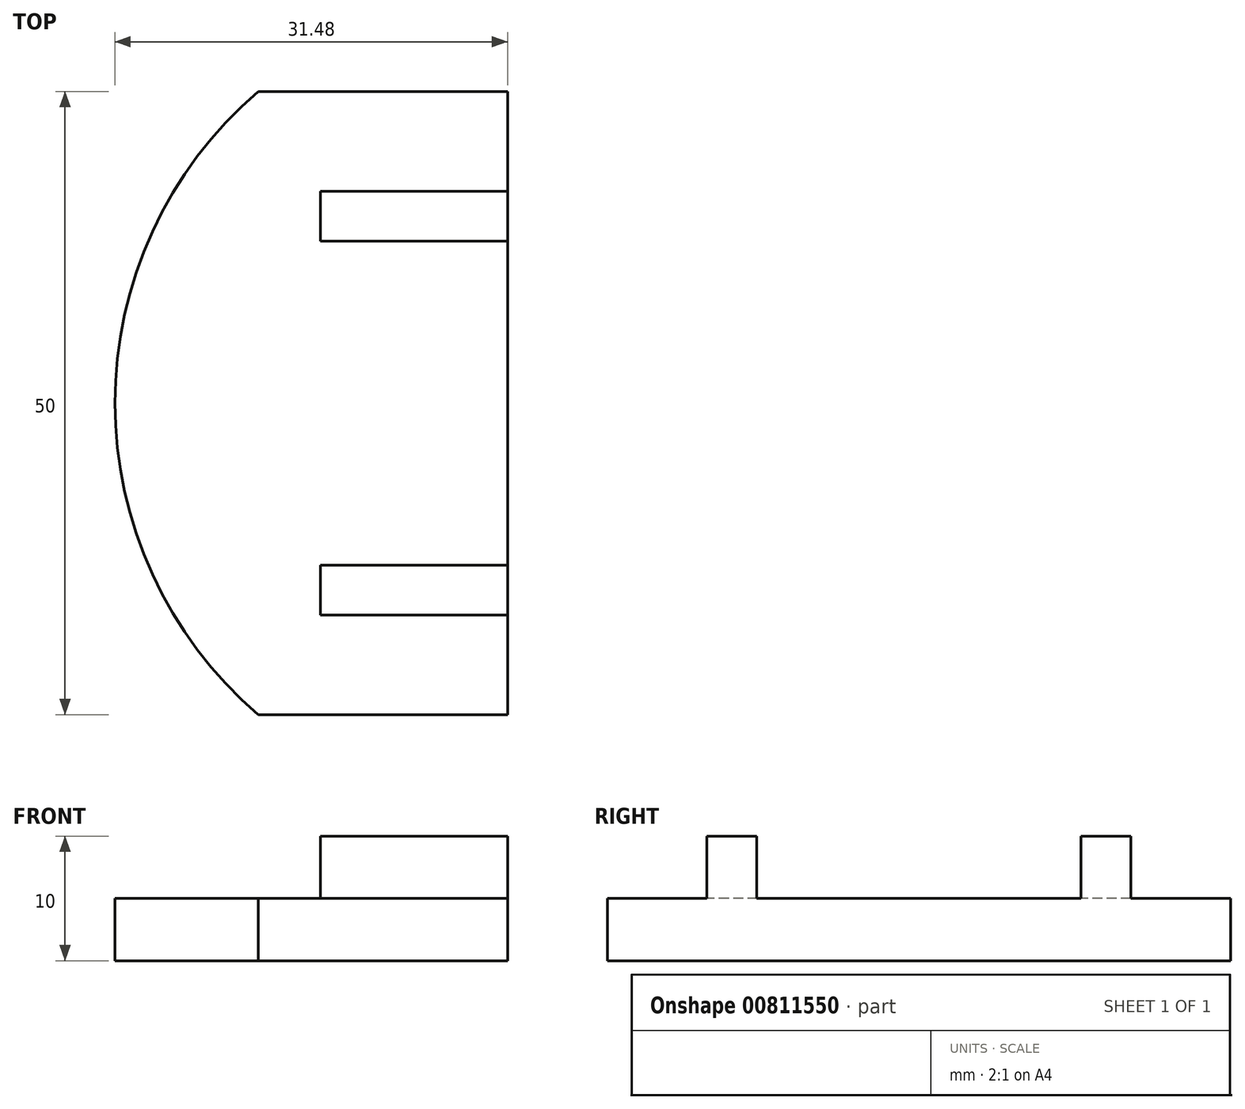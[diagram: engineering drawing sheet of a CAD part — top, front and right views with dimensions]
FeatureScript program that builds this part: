
annotation { "Feature Type Name" : "Feature", "Feature Type Description" : "" }
export const myFeature = defineFeature(function(context is Context, id is Id, definition is map)
    precondition{}
    {
        {
            var Q0;
            Q0=qCreatedBy(makeId("Top.planeOp"),FACE);
            var sketch = newSketch(context, id + "F0", { "sketchPlane" : qUnion([Q0])});
            skLineSegment(sketch, "E0.bottom", {"start": v(-10, -25) * mm, "end": v(10, -25) * mm});
            skLineSegment(sketch, "E0.top", {"start": v(-10, 25) * mm, "end": v(10, 25) * mm});
            skLineSegment(sketch, "E0.left", {"start": v(-10, -25) * mm, "end": v(-10, 25) * mm});
            skLineSegment(sketch, "E0.right", {"start": v(10, -25) * mm, "end": v(10, 25) * mm});
            skPoint(sketch, "E0.middle", {"position": v(0, 0) * mm});
            skArc(sketch, "E1", {"start": v(-10, 25) * mm, "mid": v(-21.48, 0) * mm, "end": v(-10, -25) * mm});
            skSolve(sketch);
        }
        {
            var Q0;
            Q0 = qSketchRegion(id + "F0", true);
            extrude(context, id + "F1", {"entities" : qUnion([Q0]), "depth" : 5 * mm, "offsetDistance" : 25 * mm});
        }
        {
            var Q0;
            Q0=makeQuery(id+"F1.opExtrude","CAP_FACE",FACE,{"disambiguationData":[OSD([sQuery(id+"F0.wireOp",EDGE,"E0.bottom"),sQuery(id+"F0.wireOp",EDGE,"E0.top"),sQuery(id+"F0.wireOp",EDGE,"E0.right"),sQuery(id+"F0.wireOp",EDGE,"E1")])],"isStart":false});
            var sketch = newSketch(context, id + "F2", { "sketchPlane" : qUnion([Q0])});
            skLineSegment(sketch, "E2.bottom", {"start": v(10, 17) * mm, "end": v(-5, 17) * mm});
            skLineSegment(sketch, "E2.top", {"start": v(10, 13) * mm, "end": v(-5, 13) * mm});
            skLineSegment(sketch, "E2.left", {"start": v(10, 17) * mm, "end": v(10, 13) * mm});
            skLineSegment(sketch, "E2.right", {"start": v(-5, 17) * mm, "end": v(-5, 13) * mm});
            skLineSegment(sketch, "E3.bottom", {"start": v(10, -13) * mm, "end": v(-5, -13) * mm});
            skLineSegment(sketch, "E3.top", {"start": v(10, -17) * mm, "end": v(-5, -17) * mm});
            skLineSegment(sketch, "E3.left", {"start": v(10, -13) * mm, "end": v(10, -17) * mm});
            skLineSegment(sketch, "E3.right", {"start": v(-5, -13) * mm, "end": v(-5, -17) * mm});
            skSolve(sketch);
        }
        {
            var Q0;
            Q0 = qSketchRegion(id + "F2", true);
            extrude(context, id + "F3", {"entities" : qUnion([Q0]), "operationType" : NewBodyOperationType.ADD, "depth" : 5 * mm, "offsetDistance" : 25 * mm});
        }
    });
